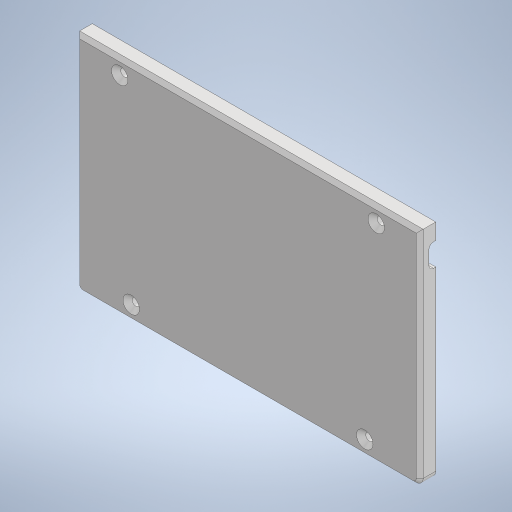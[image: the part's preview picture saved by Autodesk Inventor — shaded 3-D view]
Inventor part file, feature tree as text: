
AUTODESK INVENTOR PART (.ipt)
format: ipt  version: 2024.1 (Build 281209000, 209)  size: 330,752 bytes
history: native  units: in
note: dims shown in document units (in); Inventor stores cm internally (conversion verified against a paired STEP export)
features: extrude x7, sketch x7, fillet x3, chamfer x2
ambient origin geometry x8: Origin, YZ Plane, XZ Plane, XY Plane, X Axis, Y Axis, Z Axis, Center Point
bodies: Solid1 (feature_tree)
feature tree (19):
  extrude  "Extrusion1"  Depth=3.8287in
  extrude  "Extrusion2"  Depth=0.0984in
  extrude  "Extrusion3"  Depth=0.0984in
  extrude  "Extrusion4"  Depth=0.1969in TaperAngle=0.0deg
  fillet  "Fillet1"  Radius=0.315in
  extrude  "Extrusion5"  Depth=0.315in
  fillet  "Fillet2"  Radius=0.7874in
  extrude  "Extrusion6"  Depth=0.315in
  fillet  "Fillet3"  Radius=0.315in
  chamfer  "Chamfer1"  Distance=0.315in
  extrude  "Extrusion7"  Depth=0.5906in
  chamfer  "Chamfer2"  Distance=0.5906in
  sketch  "Sketch1"  dims[d0=5.9055in d1=3.8287in]
  sketch  "Sketch2"  dims[d2=0.2756in d3=0.0in d4=0.0984in]
  sketch  "Sketch3"  dims[d5=0.0984in d6=0.0984in]
  sketch  "Sketch4"  dims[d7=0.0984in d8=0.1969in d9=0.0in d10=0.315in]
  sketch  "Sketch5"  dims[d11=0.315in d12=0.315in d13=0.7874in]
  sketch  "Sketch6"  dims[d14=0.7874in d15=0.315in d16=0.315in]
  sketch  "Sketch7"  dims[d17=0.315in d18=0.315in d19=0.5906in d20=0.5906in d21=0.4134in d22=0.1969in d23=0.0in d24=0.126in d25=0.126in d26=0.9449in d27=0.2559in d28=0.9449in d29=0.2559in d30=0.126in d31=0.126in d32=0.748in d33=0.2559in d34=0.2559in d35=0.748in d36=0.0in d37=0.0in d38=0.1181in d39=0.1181in d40=0.2756in d41=0.3937in d42=0.0in d43=0.0in d44=0.0787in d45=0.1181in d46=0.3937in d47=0.2756in d48=0.3937in d49=0.0in d50=0.0787in d51=0.0591in d52=0.0787in d53=45.0deg d54=0.1969in d55=0.4331in d56=0.0984in d57=0.3937in d58=0.0in d59=0.0787in d60=0.0787in d61=45.0deg]
